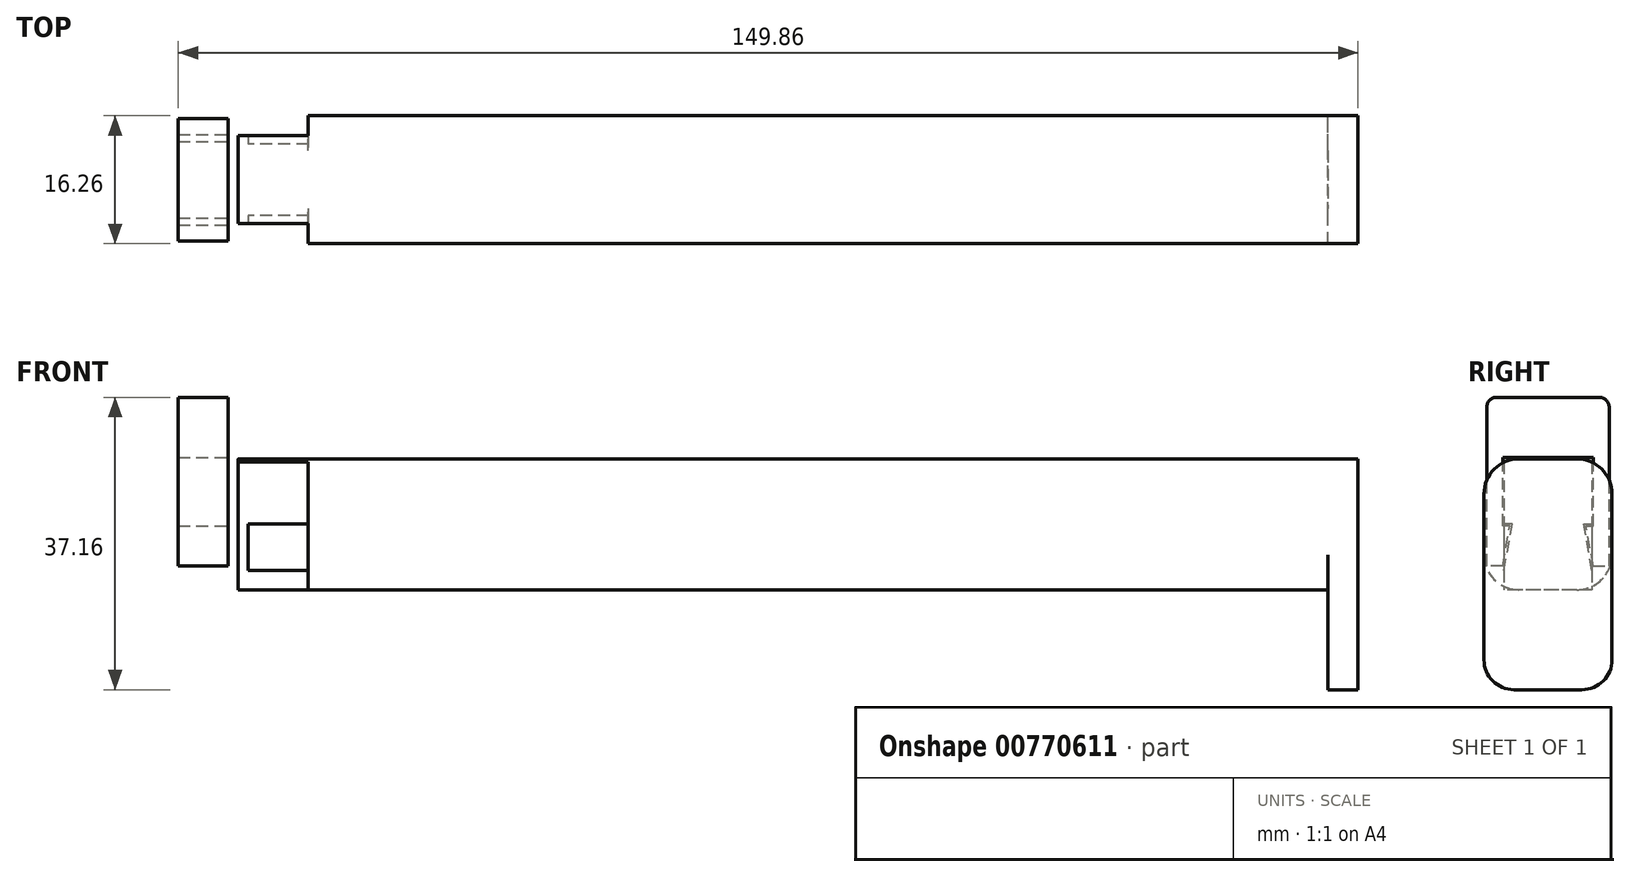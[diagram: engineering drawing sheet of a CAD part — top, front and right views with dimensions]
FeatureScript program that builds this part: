
annotation { "Feature Type Name" : "Feature", "Feature Type Description" : "" }
export const myFeature = defineFeature(function(context is Context, id is Id, definition is map)
    precondition{}
    {
        {
            var Q0;
            Q0=qCreatedBy(makeId("Top.planeOp"),FACE);
            var sketch = newSketch(context, id + "F0", { "sketchPlane" : qUnion([Q0])});
            skLineSegment(sketch, "E0.bottom", {"start": v(-64.77, 8.13) * mm, "end": v(64.77, 8.13) * mm});
            skLineSegment(sketch, "E0.top", {"start": v(-64.77, -8.13) * mm, "end": v(64.77, -8.13) * mm});
            skLineSegment(sketch, "E0.left", {"start": v(-64.77, 8.13) * mm, "end": v(-64.77, -8.13) * mm});
            skLineSegment(sketch, "E0.right", {"start": v(64.77, 8.13) * mm, "end": v(64.77, -8.13) * mm});
            skPoint(sketch, "E1", {"position": v(0, 8.13) * mm});
            skPoint(sketch, "E2", {"position": v(-64.77, 0) * mm});
            skSolve(sketch);
        }
        {
            var Q0;
            Q0 = qSketchRegion(id + "F0", true);
            extrude(context, id + "F1", {"entities" : qUnion([Q0]), "depth" : 16.64 * mm, "offsetDistance" : 25.4 * mm});
        }
        {
            var Q0;
            Q0=makeQuery(id+"F1.opExtrude","CAP_EDGE",EDGE,{"disambiguationData":[OSD([sQuery(id+"F0.wireOp",EDGE,"E0.top")])],"isStart":false});
            var Q1;
            Q1=makeQuery(id+"F1.opExtrude","CAP_EDGE",EDGE,{"disambiguationData":[OSD([sQuery(id+"F0.wireOp",EDGE,"E0.bottom")])],"isStart":false});
            var Q2;
            Q2=makeQuery(id+"F1.opExtrude","CAP_EDGE",EDGE,{"disambiguationData":[OSD([sQuery(id+"F0.wireOp",EDGE,"E0.top")])],"isStart":true});
            var Q3;
            Q3=makeQuery(id+"F1.opExtrude","CAP_EDGE",EDGE,{"disambiguationData":[OSD([sQuery(id+"F0.wireOp",EDGE,"E0.bottom")])],"isStart":true});
            fillet(context, id + "F2", {"entities" : qUnion([Q0, Q1, Q2, Q3]), "radius" : 4.44 * mm, "tangentPropagation" : true, "allowEdgeOverflow" : false});
        }
        {
            var Q0;
            Q0=makeQuery(id+"F1.opExtrude","SWEPT_FACE",FACE,{"disambiguationData":[OSD([sQuery(id+"F0.wireOp",EDGE,"E0.right")])]});
            var sketch = newSketch(context, id + "F3", { "sketchPlane" : qUnion([Q0])});
            skArc(sketch, "E3.0", {"start": v(-3.68, 16.64) * mm, "mid": v(-6.83, 15.34) * mm, "end": v(-8.13, 12.2) * mm});
            skLineSegment(sketch, "E4.0", {"start": v(3.68, 16.64) * mm, "end": v(-3.68, 16.64) * mm});
            skArc(sketch, "E5.0", {"start": v(8.13, 12.2) * mm, "mid": v(6.83, 15.34) * mm, "end": v(3.68, 16.64) * mm});
            skLineSegment(sketch, "E6", {"start": v(-8.13, 12.2) * mm, "end": v(-8.13, -8.9) * mm});
            skPoint(sketch, "E6.endSnap0", {"position": v(-8.13, 8.32) * mm});
            skLineSegment(sketch, "E7", {"start": v(-4.32, -12.7) * mm, "end": v(4.32, -12.7) * mm});
            skLineSegment(sketch, "E8", {"start": v(8.13, -8.9) * mm, "end": v(8.13, 12.2) * mm});
            skPoint(sketch, "E9.visualSharp", {"position": v(-8.13, -12.7) * mm});
            skArc(sketch, "E9.filletArc", {"start": v(-8.13, -8.9) * mm, "mid": v(-7.01, -11.58) * mm, "end": v(-4.32, -12.7) * mm});
            skPoint(sketch, "E10.visualSharp", {"position": v(8.13, -12.7) * mm});
            skArc(sketch, "E10.filletArc", {"start": v(4.32, -12.7) * mm, "mid": v(7.01, -11.58) * mm, "end": v(8.13, -8.9) * mm});
            skSolve(sketch);
        }
        {
            var Q0;
            Q0 = qSketchRegion(id + "F3", true);
            extrude(context, id + "F4", {"entities" : qUnion([Q0]), "operationType" : NewBodyOperationType.ADD, "depth" : 3.8 * mm, "offsetDistance" : 25.4 * mm});
        }
        {
            var Q0;
            Q0=makeQuery(id+"F1.opExtrude","SWEPT_FACE",FACE,{"disambiguationData":[OSD([sQuery(id+"F0.wireOp",EDGE,"E0.left")])]});
            var sketch = newSketch(context, id + "F5", { "sketchPlane" : qUnion([Q0])});
            skLineSegment(sketch, "E11", {"start": v(-8.13, 8.32) * mm, "end": v(0, 8.32) * mm, "construction": true});
            skLineSegment(sketch, "E12", {"start": v(0, 16.64) * mm, "end": v(0, 8.32) * mm, "construction": true});
            skLineSegment(sketch, "E13.bottom", {"start": v(-3.68, 16.64) * mm, "end": v(3.68, 16.64) * mm});
            skLineSegment(sketch, "E13.top", {"start": v(-5.59, 0) * mm, "end": v(5.59, 0) * mm});
            skLineSegment(sketch, "E13.left", {"start": v(-5.59, 16.2) * mm, "end": v(-5.59, 0) * mm});
            skLineSegment(sketch, "E13.right", {"start": v(5.59, 16.2) * mm, "end": v(5.59, 0) * mm});
            skArc(sketch, "E14.0", {"start": v(-3.68, 16.64) * mm, "mid": v(-4.66, 16.53) * mm, "end": v(-5.59, 16.2) * mm});
            skArc(sketch, "E15.0", {"start": v(5.59, 16.2) * mm, "mid": v(4.66, 16.53) * mm, "end": v(3.68, 16.64) * mm});
            skPoint(sketch, "E16.orphan", {"position": v(-8.13, 12.2) * mm});
            skPoint(sketch, "E17.orphan", {"position": v(8.13, 12.2) * mm});
            skSolve(sketch);
        }
        {
            var Q0;
            Q0 = qSketchRegion(id + "F5", true);
            extrude(context, id + "F6", {"entities" : qUnion([Q0]), "operationType" : NewBodyOperationType.ADD, "depth" : 8.9 * mm, "offsetDistance" : 25.4 * mm});
        }
        {
            var Q0;
            Q0=makeQuery(id+"F6.opExtrude","CAP_FACE",FACE,{"disambiguationData":[OSD([sQuery(id+"F5.wireOp",EDGE,"E13.bottom"),sQuery(id+"F5.wireOp",EDGE,"E13.top"),sQuery(id+"F5.wireOp",EDGE,"E13.left"),sQuery(id+"F5.wireOp",EDGE,"E13.right")])],"isStart":false});
            var sketch = newSketch(context, id + "F7", { "sketchPlane" : qUnion([Q0])});
            skLineSegment(sketch, "E18.bottom", {"start": v(0, 24.46) * mm, "end": v(8.13, 24.46) * mm});
            skLineSegment(sketch, "E19", {"start": v(0, 16.84) * mm, "end": v(5.74, 16.84) * mm});
            skLineSegment(sketch, "E20", {"start": v(5.74, 3.05) * mm, "end": v(4.85, 8.13) * mm});
            skLineSegment(sketch, "E21", {"start": v(4.85, 8.13) * mm, "end": v(5.74, 8.13) * mm});
            skLineSegment(sketch, "E22", {"start": v(5.74, 3.05) * mm, "end": v(7.77, 3.05) * mm});
            skLineSegment(sketch, "E23", {"start": v(7.77, 3.05) * mm, "end": v(7.77, 24.46) * mm});
            skLineSegment(sketch, "E24", {"start": v(5.74, 8.13) * mm, "end": v(5.74, 16.84) * mm});
            skLineSegment(sketch, "E25.MirrorCS", {"start": v(0, 24.46) * mm, "end": v(-8.13, 24.46) * mm});
            skLineSegment(sketch, "E26.MirrorCS", {"start": v(-7.77, 3.05) * mm, "end": v(-7.77, 24.46) * mm});
            skLineSegment(sketch, "E27.MirrorCS", {"start": v(0, 16.84) * mm, "end": v(-5.74, 16.84) * mm});
            skLineSegment(sketch, "E28.MirrorCS", {"start": v(-5.74, 8.13) * mm, "end": v(-5.74, 16.84) * mm});
            skLineSegment(sketch, "E29.MirrorCS", {"start": v(-4.85, 8.13) * mm, "end": v(-5.74, 8.13) * mm});
            skLineSegment(sketch, "E30.MirrorCS", {"start": v(-5.74, 3.05) * mm, "end": v(-4.85, 8.13) * mm});
            skLineSegment(sketch, "E31.MirrorCS", {"start": v(-5.74, 3.05) * mm, "end": v(-7.77, 3.05) * mm});
            skSolve(sketch);
        }
        {
            var Q0;
            Q0 = qSketchRegion(id + "F7", true);
            extrude(context, id + "F8", {"entities" : qUnion([Q0]), "depth" : 7.62 * mm, "offsetDistance" : 25.4 * mm, "hasSecondDirection" : true, "secondDirectionOppositeDirection" : false, "secondDirectionDepth" : 1.27 * mm});
        }
        {
            var Q0;
            Q0=makeQuery(id+"F6.opExtrude","CAP_FACE",FACE,{"disambiguationData":[OSD([sQuery(id+"F5.wireOp",EDGE,"E13.bottom"),sQuery(id+"F5.wireOp",EDGE,"E13.top"),sQuery(id+"F5.wireOp",EDGE,"E13.left"),sQuery(id+"F5.wireOp",EDGE,"E13.right")])],"isStart":false});
            var sketch = newSketch(context, id + "F9", { "sketchPlane" : qUnion([Q0])});
            skLineSegment(sketch, "E32.0", {"start": v(-4.54, 8.38) * mm, "end": v(-5.59, 8.38) * mm});
            skLineSegment(sketch, "E32.1", {"start": v(-5.59, 2.46) * mm, "end": v(-4.54, 8.38) * mm});
            skLineSegment(sketch, "E33", {"start": v(-5.59, 8.38) * mm, "end": v(-5.59, 2.46) * mm});
            skLineSegment(sketch, "E34.MirrorCS", {"start": v(4.54, 8.38) * mm, "end": v(5.59, 8.38) * mm});
            skLineSegment(sketch, "E35.MirrorCS", {"start": v(5.59, 2.46) * mm, "end": v(4.54, 8.38) * mm});
            skLineSegment(sketch, "E36.MirrorCS", {"start": v(5.59, 8.38) * mm, "end": v(5.59, 2.46) * mm});
            skSolve(sketch);
        }
        {
            var Q0;
            Q0 = qSketchRegion(id + "F9", true);
            extrude(context, id + "F10", {"entities" : qUnion([Q0]), "operationType" : NewBodyOperationType.REMOVE, "oppositeDirection" : true, "depth" : 8.9 * mm, "offsetDistance" : 25.4 * mm, "hasSecondDirection" : true, "secondDirectionOppositeDirection" : true, "secondDirectionDepth" : 1.27 * mm});
        }
        {
            var Q0;
            Q0=makeQuery(id+"F8.opExtrude","SWEPT_EDGE",EDGE,{"disambiguationData":[OSD([sQuery(id+"F7.wireOp",EDGE,"E25.MirrorCS"),sQuery(id+"F7.wireOp",EDGE,"E26.MirrorCS")])]});
            var Q1;
            Q1=makeQuery(id+"F8.opExtrude","SWEPT_EDGE",EDGE,{"disambiguationData":[OSD([sQuery(id+"F7.wireOp",EDGE,"E18.bottom"),sQuery(id+"F7.wireOp",EDGE,"E23")])]});
            fillet(context, id + "F11", {"entities" : qUnion([Q0, Q1]), "tangentPropagation" : true, "radius" : 1.27 * mm, "defaultsChanged" : true, "vertexSettings" : [], "allowEdgeOverflow" : false});
        }
    });
